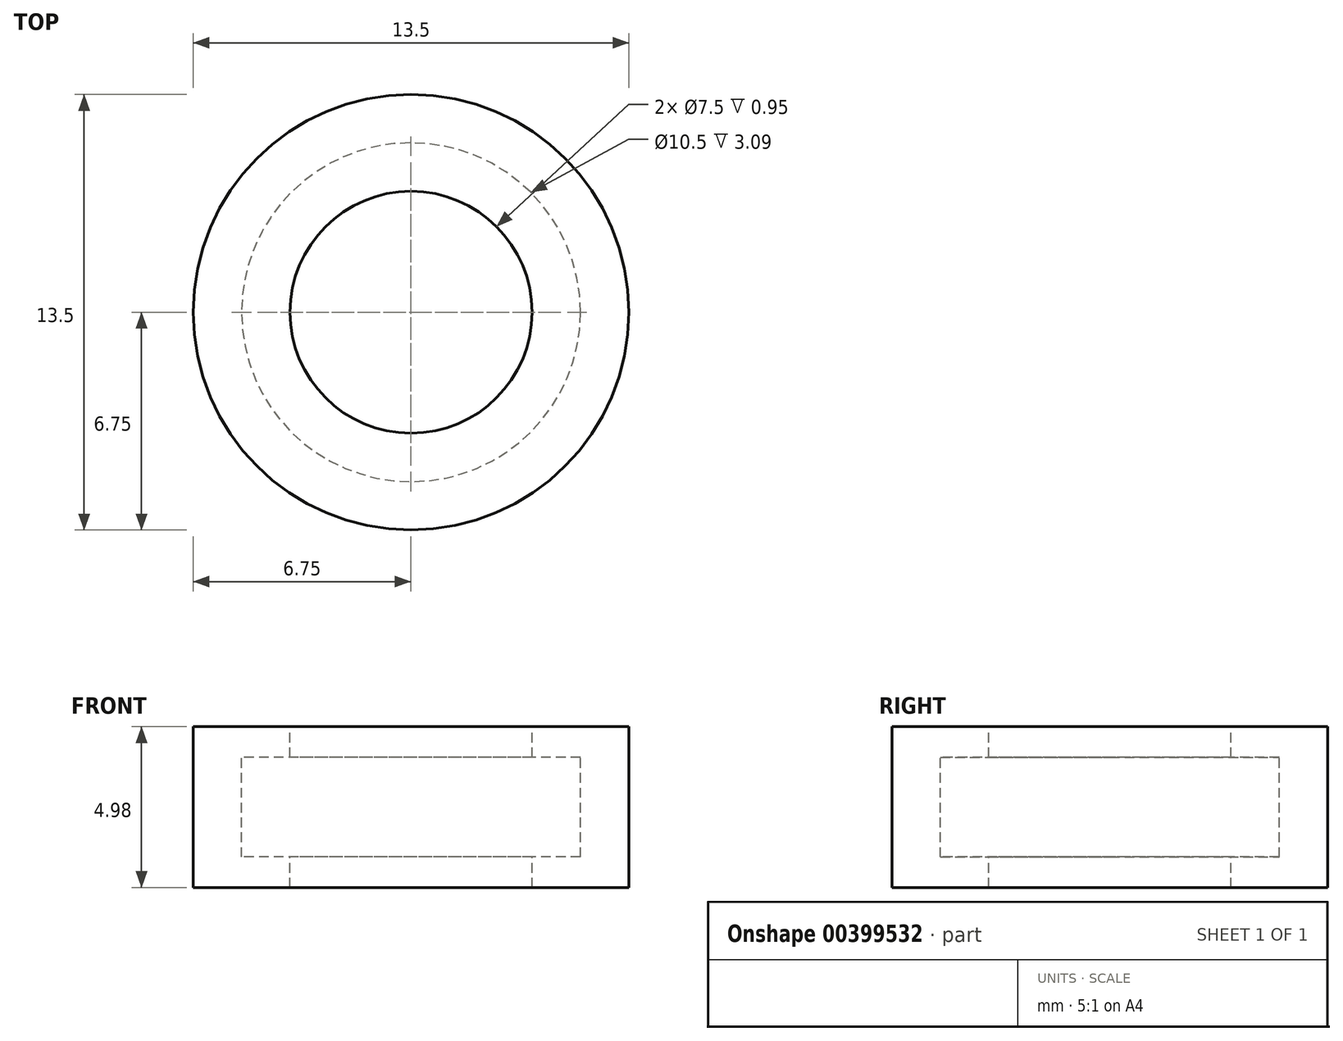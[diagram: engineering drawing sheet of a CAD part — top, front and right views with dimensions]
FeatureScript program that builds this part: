
annotation { "Feature Type Name" : "Feature", "Feature Type Description" : "" }
export const myFeature = defineFeature(function(context is Context, id is Id, definition is map)
    precondition{}
    {
        {
            var Q0;
            Q0=qCreatedBy(makeId("Front.planeOp"),FACE);
            var sketch = newSketch(context, id + "F0", { "sketchPlane" : qUnion([Q0])});
            skLineSegment(sketch, "E0.bottom", {"start": v(2.25, -2.5) * mm, "end": v(0, -2.5) * mm});
            skLineSegment(sketch, "E0.top", {"start": v(2.25, 2.5) * mm, "end": v(0, 2.5) * mm});
            skLineSegment(sketch, "E0.left", {"start": v(2.25, -2.5) * mm, "end": v(2.25, 2.5) * mm});
            skPoint(sketch, "E0.middle", {"position": v(0, 0) * mm});
            skLineSegment(sketch, "E1.bottom", {"start": v(6.75, -2.5) * mm, "end": v(3.75, -2.5) * mm});
            skLineSegment(sketch, "E1.top", {"start": v(6.75, 2.5) * mm, "end": v(3.75, 2.5) * mm});
            skLineSegment(sketch, "E1.left", {"start": v(6.75, -2.5) * mm, "end": v(6.75, 2.5) * mm});
            skLineSegment(sketch, "E2", {"start": v(0, 2.5) * mm, "end": v(0, -2.5) * mm, "construction": true});
            skPoint(sketch, "E0.right.start.orphan", {"position": v(-2.25, -2.5) * mm});
            skPoint(sketch, "E1.right.end.orphan", {"position": v(-6.75, 2.5) * mm});
            skPoint(sketch, "E1.right.start.orphan", {"position": v(-6.75, -2.5) * mm});
            skPoint(sketch, "E3.orphan", {"position": v(-2.25, 2.5) * mm});
            skLineSegment(sketch, "E4.bottom", {"start": v(3.75, 1.5) * mm, "end": v(5.2, 1.5) * mm});
            skLineSegment(sketch, "E4.top", {"start": v(3.75, -1.5) * mm, "end": v(5.2, -1.5) * mm});
            skLineSegment(sketch, "E4.left", {"start": v(2.25, 1.5) * mm, "end": v(2.25, -1.5) * mm});
            skLineSegment(sketch, "E4.right", {"start": v(5.2, 1.5) * mm, "end": v(5.2, -1.5) * mm});
            skLineSegment(sketch, "E5.bottom", {"start": v(3.75, 1.54) * mm, "end": v(5.25, 1.54) * mm});
            skLineSegment(sketch, "E5.top", {"start": v(3.75, -1.54) * mm, "end": v(5.25, -1.54) * mm});
            skLineSegment(sketch, "E5.left", {"start": v(2.25, 1.54) * mm, "end": v(2.25, -1.54) * mm});
            skLineSegment(sketch, "E5.right", {"start": v(5.25, 1.54) * mm, "end": v(5.25, -1.54) * mm});
            skLineSegment(sketch, "E6", {"start": v(3.75, 2.5) * mm, "end": v(3.75, 1.54) * mm});
            skPoint(sketch, "E6.startSnap0", {"position": v(3.75, 1.54) * mm});
            skLineSegment(sketch, "E7.trimOffspring", {"start": v(3.75, -1.54) * mm, "end": v(3.75, -2.5) * mm});
            skLineSegment(sketch, "E8", {"start": v(3.7, 2.5) * mm, "end": v(3.7, 1.5) * mm});
            skLineSegment(sketch, "E9", {"start": v(3.75, 1.5) * mm, "end": v(3.7, 1.5) * mm});
            skLineSegment(sketch, "E10", {"start": v(3.7, -1.5) * mm, "end": v(3.75, -1.5) * mm});
            skLineSegment(sketch, "E11.trimOffspring", {"start": v(3.7, -1.5) * mm, "end": v(3.7, -2.5) * mm});
            skLineSegment(sketch, "E12.trimOffspring", {"start": v(3.7, 2.5) * mm, "end": v(0, 2.5) * mm});
            skLineSegment(sketch, "E13.trimOffspring", {"start": v(3.7, -2.5) * mm, "end": v(0, -2.5) * mm});
            skSolve(sketch);
        }
        {
            var Q0;
            Q0=qSketchRegion(id+"F0",true);
            var Q1;
            Q1=sQuery(id+"F0.wireOp",EDGE,"E2");
            revolve(context, id + "F1", {"entities" : qUnion([Q0]), "axis" : qUnion([Q1]), "revolveType" : RevolveType.FULL});
        }
        {
            var Q0;
            Q0=makeQuery(id+"F1.opRevolve","SWEPT_BODY",BODY,{"disambiguationData":[OSD([sQuery(id+"F0.wireOp",EDGE,"E0.left"),sQuery(id+"F0.wireOp",EDGE,"E4.bottom"),sQuery(id+"F0.wireOp",EDGE,"E4.top"),sQuery(id+"F0.wireOp",EDGE,"E4.right"),sQuery(id+"F0.wireOp",EDGE,"E5.left"),sQuery(id+"F0.wireOp",EDGE,"E8"),sQuery(id+"F0.wireOp",EDGE,"E9"),sQuery(id+"F0.wireOp",EDGE,"E10"),sQuery(id+"F0.wireOp",EDGE,"E11.trimOffspring"),sQuery(id+"F0.wireOp",EDGE,"E12.trimOffspring"),sQuery(id+"F0.wireOp",EDGE,"E13.trimOffspring")])]});
            deleteBodies(context, id + "F2", {"entities" : qUnion([Q0])});
        }
    });
